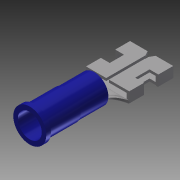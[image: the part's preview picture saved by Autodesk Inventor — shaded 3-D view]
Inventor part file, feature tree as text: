
AUTODESK INVENTOR PART (.ipt)
format: ipt  version: 2014 (Build 180170000, 170)  size: 340,480 bytes
history: native  units: in
note: dims shown in document units (in); Inventor stores cm internally (conversion verified against a paired STEP export)
features: sketch x11, projected_geometry x11, extrude x7, plane x2, shell x1, revolve x1, loft x1, fillet x1, chamfer x1
ambient origin geometry x8: Origin, YZ Plane, XZ Plane, XY Plane, X Axis, Y Axis, Z Axis, Center Point
bodies: Solid1 (feature_tree), Solid2 (feature_tree)
feature tree (36):
  extrude  "Extrusion1"  Depth=0.1965in TaperAngle=0.0deg
  extrude  "Extrusion2"  Depth=0.254in TaperAngle=0.0deg
  extrude  "Extrusion3"  Depth=0.033in TaperAngle=0.0deg
  shell  "Shell1"  Thickness=0.0185in
  extrude  "Extrusion4"  Depth=0.0185in
  revolve  "Revolution1"  [1 undecoded]
  plane  "Work Plane1"
  sketch  "Sketch6"  dims[d15=0.4in d16=0.018in]
  plane  "Work Plane2"
  extrude  "Extrusion5"  Depth=0.018in
  loft  "Loft1"
  fillet  "Fillet1"  Radius=0.018in
  extrude  "Extrusion6"  Depth=0.018in
  extrude  "Extrusion7"  Depth=0.307in TaperAngle=0.0deg
  chamfer  "Chamfer1"  Distance=0.3937in Angle=90.0deg
  sketch  "Sketch1"  dims[d0=0.1965in d1=0.1965in d2=0.0in]
  sketch  "Sketch2"  dims[d3=0.204in d4=0.254in d5=0.0in]
  projected_geometry  "Projected Loop1"
  sketch  "Sketch3"  dims[d6=0.23in d7=0.033in d8=0.0in d9=0.0185in]
  projected_geometry  "Projected Loop2"
  sketch  "Sketch4"  dims[d10=0.033in d11=0.0in d12=0.0185in]
  projected_geometry  "Projected Loop3"
  sketch  "Sketch5"  dims[d13=90.0deg d14=-0.0625in]
  sketch  "Sketch7"  dims[d17=0.3015in d18=0.018in d19=0.018in]
  sketch  "Sketch8"  dims[d20=0.018in d21=0.037in]
  projected_geometry  "Projected Loop4"
  sketch  "Sketch9"  dims[d22=0.02in d23=0.307in d24=0.0in d29=0.3937in d30=90.0deg]
  projected_geometry  "Projected Loop5"
  sketch  "Sketch10"  dims[d31=0.0in d32=90.0deg]
  projected_geometry  "Projected Loop6"
  projected_geometry  "Projected Loop7"
  sketch  "Sketch11"  dims[d33=0.02in d34=0.1in d36=0.178in d37=0.307in d38=0.0in d39=0.05in d40=0.0in d41=0.003in d42=0.125in d43=45.0deg]
  projected_geometry  "Projected Loop8"
  projected_geometry  "Projected Loop9"
  projected_geometry  "Project Cut Edges1"
  projected_geometry  "Project Cut Edges2"
note: 1 required parameter value undecoded (feature->parameter linkage not recoverable at this tier; creation-order binding heuristic only, values carry confidence <= 0.55)
